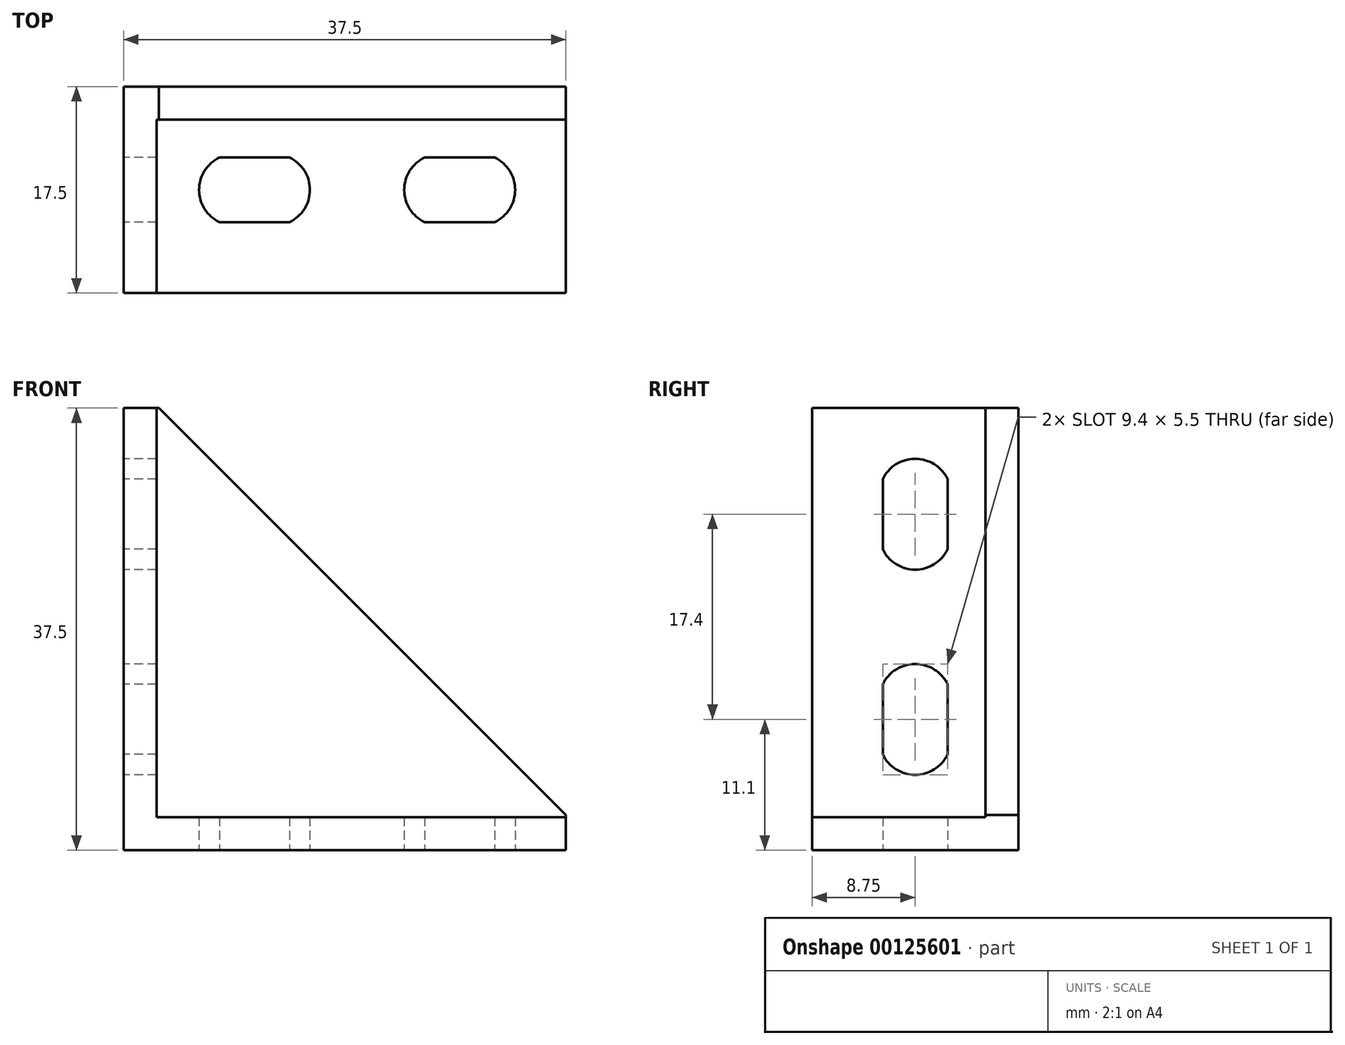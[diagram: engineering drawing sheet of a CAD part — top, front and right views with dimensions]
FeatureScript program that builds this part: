
annotation { "Feature Type Name" : "Feature", "Feature Type Description" : "" }
export const myFeature = defineFeature(function(context is Context, id is Id, definition is map)
    precondition{}
    {
        {
            var Q0;
            Q0=qCreatedBy(makeId("Front.planeOp"),FACE);
            var sketch = newSketch(context, id + "F0", { "sketchPlane" : qUnion([Q0])});
            skLineSegment(sketch, "E0", {"start": v(0, 0) * mm, "end": v(37.5, 0) * mm});
            skLineSegment(sketch, "E1", {"start": v(37.5, 0) * mm, "end": v(37.5, 2.8) * mm});
            skLineSegment(sketch, "E2", {"start": v(37.5, 2.8) * mm, "end": v(2.8, 2.8) * mm});
            skLineSegment(sketch, "E3", {"start": v(2.8, 2.8) * mm, "end": v(2.8, 37.5) * mm});
            skLineSegment(sketch, "E4", {"start": v(2.8, 37.5) * mm, "end": v(0, 37.5) * mm});
            skLineSegment(sketch, "E5", {"start": v(0, 37.5) * mm, "end": v(0, 0) * mm});
            skLineSegment(sketch, "E6", {"start": v(2.8, 37.5) * mm, "end": v(3, 37.5) * mm});
            skLineSegment(sketch, "E7", {"start": v(3, 37.5) * mm, "end": v(37.5, 3) * mm});
            skLineSegment(sketch, "E8", {"start": v(37.5, 3) * mm, "end": v(37.5, 2.8) * mm});
            skSolve(sketch);
        }
        {
            var Q0;
            Q0=makeQuery(id+"F0.imprint","IMPRINT",FACE,{"disambiguationData":[TD([[makeQuery(id+"F0.imprint","IMPRINT",EDGE,{"derivedFrom":sQuery(id+"F0.wireOp",EDGE,"E0")}),1.0]])]});
            extrude(context, id + "F1", {"entities" : qUnion([Q0]), "depth" : 17.5 * mm});
        }
        {
            var Q0;
            Q0=makeQuery(id+"F0.imprint","IMPRINT",FACE,{"disambiguationData":[TD([[makeQuery(id+"F0.imprint","IMPRINT",EDGE,{"derivedFrom":sQuery(id+"F0.wireOp",EDGE,"E2")}),-1.0]])]});
            extrude(context, id + "F2", {"entities" : qUnion([Q0]), "operationType" : NewBodyOperationType.ADD, "depth" : 2.8 * mm});
        }
        {
            var Q0;
            Q0=makeQuery(id+"F1.opExtrude","SWEPT_FACE",FACE,{"disambiguationData":[OSD([sQuery(id+"F0.wireOp",EDGE,"E5")])]});
            var sketch = newSketch(context, id + "F3", { "sketchPlane" : qUnion([Q0])});
            skLineSegment(sketch, "E9", {"start": v(6, 31.47) * mm, "end": v(6, 25.53) * mm});
            skLineSegment(sketch, "E10", {"start": v(11.5, 31.47) * mm, "end": v(11.5, 25.53) * mm});
            skArc(sketch, "E11", {"start": v(11.5, 31.47) * mm, "mid": v(8.75, 33.2) * mm, "end": v(6, 31.47) * mm});
            skLineSegment(sketch, "E12", {"start": v(6, 28.5) * mm, "end": v(11.5, 28.5) * mm, "construction": true});
            skArc(sketch, "E13.MirrorCS", {"start": v(11.5, 25.53) * mm, "mid": v(8.75, 23.8) * mm, "end": v(6, 25.53) * mm});
            skLineSegment(sketch, "E14.1.0.0", {"start": v(6, 14.07) * mm, "end": v(6, 8.13) * mm});
            skArc(sketch, "E14.1.0.1", {"start": v(11.5, 14.07) * mm, "mid": v(8.75, 15.8) * mm, "end": v(6, 14.07) * mm});
            skLineSegment(sketch, "E14.1.0.2", {"start": v(11.5, 14.07) * mm, "end": v(11.5, 8.13) * mm});
            skArc(sketch, "E14.1.0.3", {"start": v(11.5, 8.13) * mm, "mid": v(8.75, 6.4) * mm, "end": v(6, 8.13) * mm});
            skLineSegment(sketch, "E14.direction1", {"start": v(8.75, 30.15) * mm, "end": v(8.75, 12.75) * mm, "construction": true});
            skPoint(sketch, "E15", {"position": v(6, 11.1) * mm});
            skLineSegment(sketch, "E16", {"start": v(6, 11.1) * mm, "end": v(11.5, 11.1) * mm, "construction": true});
            skPoint(sketch, "E17", {"position": v(8.75, 11.1) * mm});
            skSolve(sketch);
        }
        {
            var Q0;
            Q0=makeQuery(id+"F3.imprint","IMPRINT",FACE,{"disambiguationData":[TD([[makeQuery(id+"F3.imprint","IMPRINT",EDGE,{"derivedFrom":sQuery(id+"F3.wireOp",EDGE,"E9")}),1.0]])]});
            var Q1;
            Q1=makeQuery(id+"F3.imprint","IMPRINT",FACE,{"disambiguationData":[TD([[makeQuery(id+"F3.imprint","IMPRINT",EDGE,{"derivedFrom":sQuery(id+"F3.wireOp",EDGE,"E14.1.0.0")}),1.0]])]});
            var Q2;
            Q2=makeQuery(id+"F1.opExtrude","SWEPT_FACE",FACE,{"disambiguationData":[OSD([sQuery(id+"F0.wireOp",EDGE,"E3")])]});
            extrude(context, id + "F4", {"entities" : qUnion([Q0, Q1]), "operationType" : NewBodyOperationType.REMOVE, "endBound" : BoundingType.UP_TO_SURFACE, "oppositeDirection" : true, "endBoundEntityFace" : qUnion([Q2]), "depth" : 2.8 * mm});
        }
        {
            var Q0;
            Q0=makeQuery(id+"F1.opExtrude","SWEPT_FACE",FACE,{"disambiguationData":[OSD([sQuery(id+"F0.wireOp",EDGE,"E0")])]});
            var sketch = newSketch(context, id + "F5", { "sketchPlane" : qUnion([Q0])});
            skLineSegment(sketch, "E18", {"start": v(8.13, 6) * mm, "end": v(14.07, 6) * mm});
            skLineSegment(sketch, "E19", {"start": v(8.13, 11.5) * mm, "end": v(14.07, 11.5) * mm});
            skArc(sketch, "E20", {"start": v(8.13, 11.5) * mm, "mid": v(6.4, 8.75) * mm, "end": v(8.13, 6) * mm});
            skLineSegment(sketch, "E21", {"start": v(11.1, 6) * mm, "end": v(11.1, 11.5) * mm, "construction": true});
            skArc(sketch, "E22.MirrorCS", {"start": v(14.07, 11.5) * mm, "mid": v(15.8, 8.75) * mm, "end": v(14.07, 6) * mm});
            skLineSegment(sketch, "E23.1.0.0", {"start": v(25.53, 6) * mm, "end": v(31.47, 6) * mm});
            skArc(sketch, "E23.1.0.1", {"start": v(25.53, 11.5) * mm, "mid": v(23.8, 8.75) * mm, "end": v(25.53, 6) * mm});
            skLineSegment(sketch, "E23.1.0.2", {"start": v(25.53, 11.5) * mm, "end": v(31.47, 11.5) * mm});
            skArc(sketch, "E23.1.0.3", {"start": v(31.47, 11.5) * mm, "mid": v(33.2, 8.75) * mm, "end": v(31.47, 6) * mm});
            skLineSegment(sketch, "E23.direction1", {"start": v(9.45, 8.75) * mm, "end": v(26.85, 8.75) * mm, "construction": true});
            skPoint(sketch, "E24", {"position": v(11.1, 8.75) * mm});
            skSolve(sketch);
        }
        {
            var Q0;
            Q0=makeQuery(id+"F5.imprint","IMPRINT",FACE,{"disambiguationData":[TD([[makeQuery(id+"F5.imprint","IMPRINT",EDGE,{"derivedFrom":sQuery(id+"F5.wireOp",EDGE,"E23.1.0.0")}),1.0]])]});
            var Q1;
            Q1=makeQuery(id+"F5.imprint","IMPRINT",FACE,{"disambiguationData":[TD([[makeQuery(id+"F5.imprint","IMPRINT",EDGE,{"derivedFrom":sQuery(id+"F5.wireOp",EDGE,"E18")}),1.0]])]});
            var Q2;
            Q2=makeQuery(id+"F1.opExtrude","SWEPT_FACE",FACE,{"disambiguationData":[OSD([sQuery(id+"F0.wireOp",EDGE,"E2")])]});
            extrude(context, id + "F6", {"entities" : qUnion([Q0, Q1]), "operationType" : NewBodyOperationType.REMOVE, "endBound" : BoundingType.UP_TO_SURFACE, "oppositeDirection" : true, "endBoundEntityFace" : qUnion([Q2]), "depth" : 25 * mm});
        }
    });
